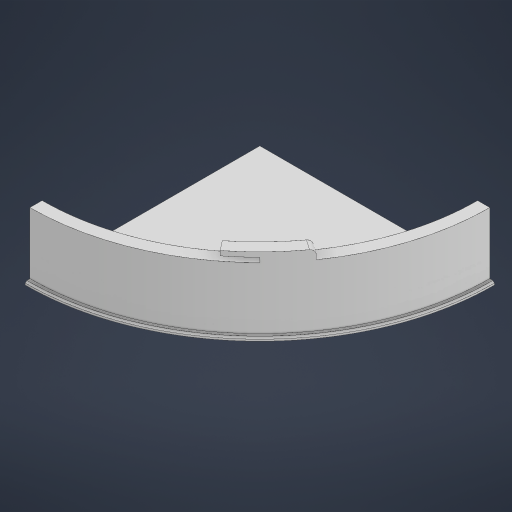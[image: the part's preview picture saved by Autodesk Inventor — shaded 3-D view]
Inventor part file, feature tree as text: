
AUTODESK INVENTOR PART (.ipt)
format: ipt  version: 2024 (Build 280153000, 153)  size: 278,016 bytes
history: native  units: in
note: dims shown in document units (in); Inventor stores cm internally (conversion verified against a paired STEP export)
features: sketch x6, extrude x6, projected_geometry x6, chamfer x2, fillet x2, draft x1
ambient origin geometry x8: Origin, YZ Plane, XZ Plane, XY Plane, X Axis, Y Axis, Z Axis, Center Point
bodies: Solid1 (feature_tree)
feature tree (23):
  sketch  "Sketch1"  dims[d0=12.0in d1=0.1181in d2=0.7874in d3=0.0in]
  extrude  "Extrusion1"  Depth=0.1181in
  chamfer  "Chamfer1"  Distance=0.7874in
  extrude  "Extrusion3"  Depth=1.5748in
  draft  "FaceDraft1"
  fillet  "Fillet1"  Radius=1.5748in
  chamfer  "Chamfer2"  Distance=0.125in
  extrude  "Extrusion4"  TaperAngle=60.0deg  [1 undecoded]
  extrude  "Extrusion5"  Depth=0.2087in TaperAngle=0.0deg
  fillet  "Fillet2"  Radius=0.3573in
  extrude  "Extrusion6"  Depth=0.2087in TaperAngle=0.0deg
  extrude  "Extrusion7"  Depth=0.125in
  sketch  "Sketch2"  dims[d4=2.625in d5=0.125in d6=15.0deg d9=0.1181in d10=1.5748in d11=0.0in]
  projected_geometry  "Projected Loop1"
  sketch  "Sketch3"  dims[d12=-0.0481in]
  projected_geometry  "Projected Loop2"
  sketch  "Sketch4"  dims[d13=0.125in d14=0.0394in d15=0.125in d16=0.1374in]
  projected_geometry  "Projected Loop3"
  projected_geometry  "Projected Loop4"
  sketch  "Sketch5"  dims[d17=45.0deg d18=60.0deg]
  projected_geometry  "Projected Loop5"
  sketch  "Sketch6"  dims[d19=0.2405in d20=0.1181in d21=0.0in d22=0.3573in d23=0.1181in d24=0.0in d25=0.125in d26=0.3937in d27=0.9843in d28=0.3937in d29=2.3622in d30=0.1969in d31=0.0in d32=0.4055in d33=0.4055in d34=0.9843in d35=2.3622in d36=0.2087in d37=0.0in]
  projected_geometry  "Projected Loop6"
note: 1 required parameter value undecoded (feature->parameter linkage not recoverable at this tier; creation-order binding heuristic only, values carry confidence <= 0.55)
